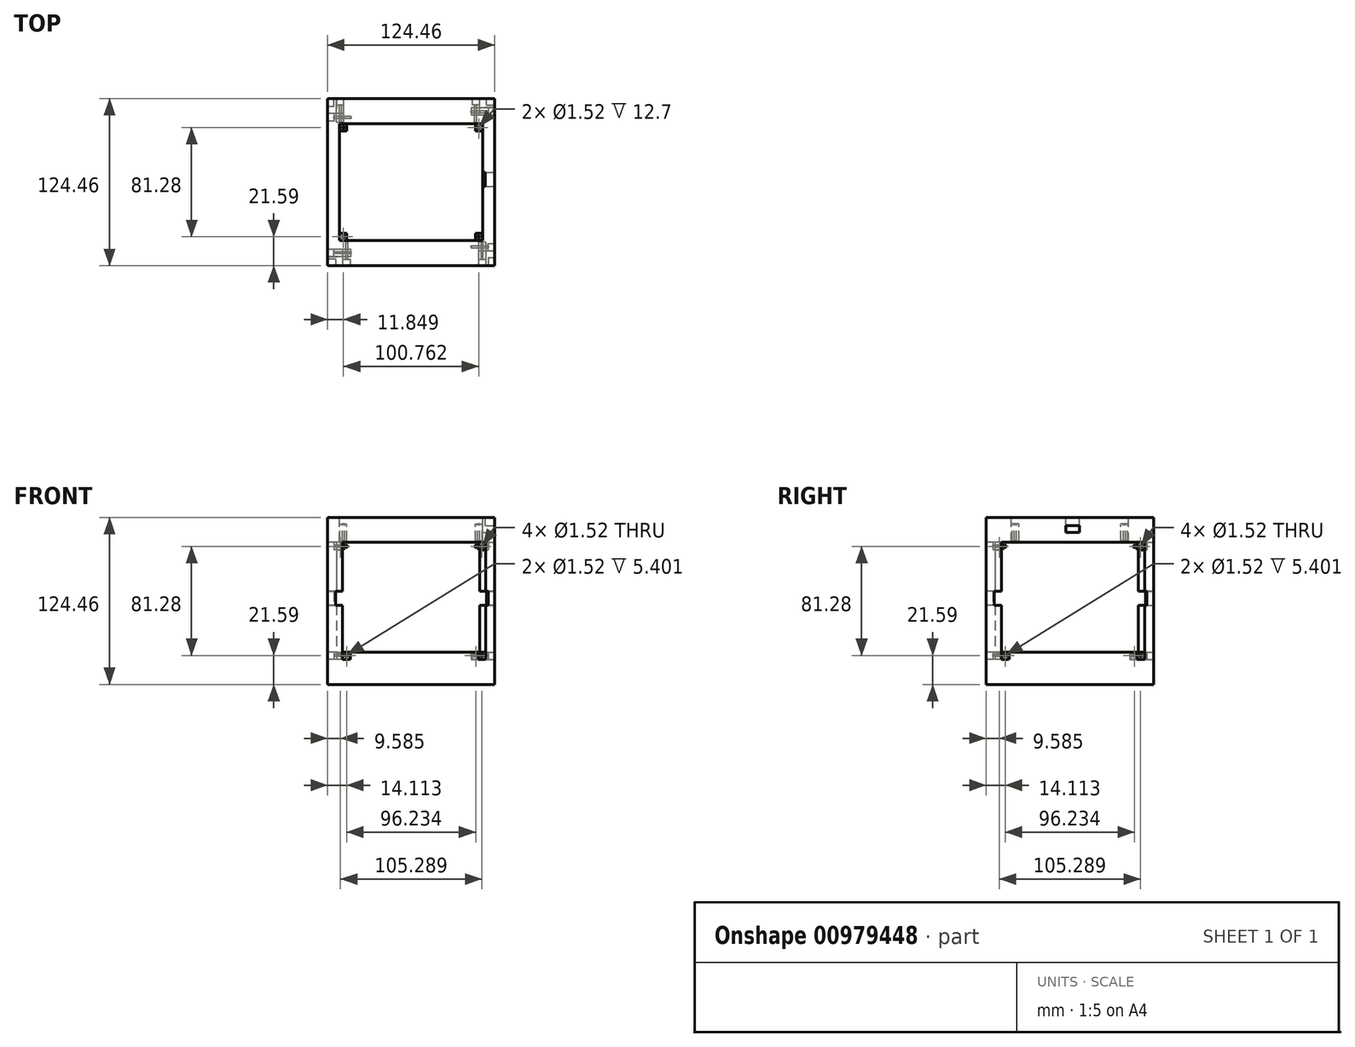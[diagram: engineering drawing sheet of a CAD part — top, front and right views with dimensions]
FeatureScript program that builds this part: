
annotation { "Feature Type Name" : "Feature", "Feature Type Description" : "" }
export const myFeature = defineFeature(function(context is Context, id is Id, definition is map)
    precondition{}
    {
        {
            var Q0;
            Q0=qCreatedBy(makeId("Top.planeOp"),FACE);
            var sketch = newSketch(context, id + "F0", { "sketchPlane" : qUnion([Q0])});
            skLineSegment(sketch, "E0.bottom", {"start": v(62.23, -62.23) * mm, "end": v(-62.23, -62.23) * mm});
            skLineSegment(sketch, "E0.top", {"start": v(62.23, 62.23) * mm, "end": v(-62.23, 62.23) * mm});
            skLineSegment(sketch, "E0.left", {"start": v(62.23, -62.23) * mm, "end": v(62.23, 62.23) * mm});
            skLineSegment(sketch, "E0.right", {"start": v(-62.23, -62.23) * mm, "end": v(-62.23, 62.23) * mm});
            skSolve(sketch);
        }
        {
            var Q0;
            Q0=makeQuery(id+"F0.imprint","IMPRINT",FACE,{"disambiguationData":[TD([[makeQuery(id+"F0.imprint","IMPRINT",EDGE,{"derivedFrom":sQuery(id+"F0.wireOp",EDGE,"E0.bottom")}),-1.0]])]});
            extrude(context, id + "F1", {"entities" : qUnion([Q0]), "depth" : 124.46 * mm, "offsetDistance" : 25.4 * mm});
        }
        {
            var Q0;
            Q0=makeQuery(id+"F1.opExtrude","CAP_FACE",FACE,{"disambiguationData":[OSD([sQuery(id+"F0.wireOp",EDGE,"E0.bottom"),sQuery(id+"F0.wireOp",EDGE,"E0.top"),sQuery(id+"F0.wireOp",EDGE,"E0.left"),sQuery(id+"F0.wireOp",EDGE,"E0.right")])],"isStart":false});
            var sketch = newSketch(context, id + "F2", { "sketchPlane" : qUnion([Q0])});
            skLineSegment(sketch, "E1.bottom", {"start": v(-52.92, 43.18) * mm, "end": v(52.92, 43.18) * mm});
            skLineSegment(sketch, "E1.top", {"start": v(-52.92, -43.18) * mm, "end": v(52.92, -43.18) * mm});
            skLineSegment(sketch, "E1.left", {"start": v(-52.92, 43.18) * mm, "end": v(-52.92, -43.18) * mm});
            skLineSegment(sketch, "E1.right", {"start": v(52.92, 43.18) * mm, "end": v(52.92, -43.18) * mm});
            skPoint(sketch, "E1.middle", {"position": v(0, 0) * mm});
            skCircle(sketch, "E2", {"center": v(-50.38, -40.64) * mm, "radius": 0.76 * mm});
            skCircle(sketch, "E3.MirrorC", {"center": v(50.38, -40.64) * mm, "radius": 0.76 * mm});
            skCircle(sketch, "E4.MirrorC", {"center": v(-50.38, 40.64) * mm, "radius": 0.76 * mm});
            skCircle(sketch, "E5.MirrorC", {"center": v(50.38, 40.64) * mm, "radius": 0.76 * mm});
            skLineSegment(sketch, "E6.0", {"start": v(-53.32, 43.58) * mm, "end": v(-53.32, -43.58) * mm});
            skLineSegment(sketch, "E6.1", {"start": v(-53.32, 43.58) * mm, "end": v(53.32, 43.58) * mm});
            skLineSegment(sketch, "E6.2", {"start": v(53.32, 43.58) * mm, "end": v(53.32, -43.58) * mm});
            skLineSegment(sketch, "E6.3", {"start": v(-53.32, -43.58) * mm, "end": v(53.32, -43.58) * mm});
            skLineSegment(sketch, "E7.top", {"start": v(53.32, -38.1) * mm, "end": v(47.84, -38.1) * mm});
            skLineSegment(sketch, "E7.right", {"start": v(47.84, -43.58) * mm, "end": v(47.84, -38.1) * mm});
            skLineSegment(sketch, "E8.MirrorCS", {"start": v(47.84, 43.58) * mm, "end": v(47.84, 38.1) * mm});
            skLineSegment(sketch, "E9.MirrorCS", {"start": v(53.32, 38.1) * mm, "end": v(47.84, 38.1) * mm});
            skLineSegment(sketch, "E10.MirrorCS", {"start": v(-53.32, -38.1) * mm, "end": v(-47.84, -38.1) * mm});
            skLineSegment(sketch, "E11.MirrorCS", {"start": v(-47.84, -43.58) * mm, "end": v(-47.84, -38.1) * mm});
            skLineSegment(sketch, "E12.MirrorCS", {"start": v(-53.32, 38.1) * mm, "end": v(-47.84, 38.1) * mm});
            skLineSegment(sketch, "E13.MirrorCS", {"start": v(-47.84, 43.58) * mm, "end": v(-47.84, 38.1) * mm});
            skLineSegment(sketch, "E14.MirrorCS", {"start": v(51.04, 6.8) * mm, "end": v(54.8, 6.8) * mm});
            skLineSegment(sketch, "E15.MirrorCS", {"start": v(51.04, -3.13) * mm, "end": v(55.2, -3.13) * mm});
            skLineSegment(sketch, "E16.MirrorCS", {"start": v(51.04, -2.73) * mm, "end": v(54.8, -2.73) * mm});
            skLineSegment(sketch, "E17.MirrorCS", {"start": v(55.2, 7.2) * mm, "end": v(55.2, -3.13) * mm});
            skLineSegment(sketch, "E18.MirrorCS", {"start": v(51.04, 7.2) * mm, "end": v(55.2, 7.2) * mm});
            skLineSegment(sketch, "E19.MirrorCS", {"start": v(54.8, 6.8) * mm, "end": v(54.8, -2.73) * mm});
            skPoint(sketch, "E20.MirrorP", {"position": v(52.92, 2.03) * mm});
            skLineSegment(sketch, "E21.bottom", {"start": v(-62.23, -62.23) * mm, "end": v(62.23, -62.23) * mm});
            skLineSegment(sketch, "E21.top", {"start": v(-62.23, 62.23) * mm, "end": v(62.23, 62.23) * mm});
            skLineSegment(sketch, "E21.left", {"start": v(-62.23, -62.23) * mm, "end": v(-62.23, 62.23) * mm});
            skLineSegment(sketch, "E21.right", {"start": v(62.23, -62.23) * mm, "end": v(62.23, 62.23) * mm});
            skSolve(sketch);
        }
        {
            var Q0;
            Q0=makeQuery(id+"F2.imprint","IMPRINT",FACE,{"disambiguationData":[TD([[makeQuery(id+"F2.imprint","IMPRINT",EDGE,{"derivedFrom":sQuery(id+"F2.wireOp",EDGE,"E2")}),-1.0]])]});
            var Q1;
            {var subQ5=sQuery(id+"F2.wireOp",EDGE,"E1.left");var subQ6=sQuery(id+"F2.wireOp",EDGE,"E1.top");var subQ7=makeQuery(id+"F2.imprint","INTERSECT",VERTEX,{"derivedFrom":[subQ6,subQ5]});Q1=makeQuery(id+"F2.imprint","IMPRINT",FACE,{"disambiguationData":[TD([[makeQuery(id+"F2.imprint","IMPRINT",EDGE,{"disambiguationData":[TD([[subQ7,-1.0]])],"derivedFrom":subQ6}),-1.0]])]});}
            var Q2;
            {var subQ7=sQuery(id+"F2.wireOp",EDGE,"E1.right");var subQ8=sQuery(id+"F2.wireOp",EDGE,"E1.top");var subQ9=makeQuery(id+"F2.imprint","INTERSECT",VERTEX,{"derivedFrom":[subQ8,subQ7]});Q2=makeQuery(id+"F2.imprint","IMPRINT",FACE,{"disambiguationData":[TD([[makeQuery(id+"F2.imprint","IMPRINT",EDGE,{"disambiguationData":[TD([[subQ9,1.0]])],"derivedFrom":subQ8}),-1.0]])]});}
            var Q3;
            Q3=makeQuery(id+"F2.imprint","IMPRINT",FACE,{"disambiguationData":[TD([[makeQuery(id+"F2.imprint","IMPRINT",EDGE,{"derivedFrom":sQuery(id+"F2.wireOp",EDGE,"E3.MirrorC")}),1.0]])]});
            var Q4;
            {var subQ7=sQuery(id+"F2.wireOp",EDGE,"E1.right");var subQ8=sQuery(id+"F2.wireOp",EDGE,"E1.bottom");var subQ9=makeQuery(id+"F2.imprint","INTERSECT",VERTEX,{"derivedFrom":[subQ8,subQ7]});Q4=makeQuery(id+"F2.imprint","IMPRINT",FACE,{"disambiguationData":[TD([[makeQuery(id+"F2.imprint","IMPRINT",EDGE,{"disambiguationData":[TD([[subQ9,1.0]])],"derivedFrom":subQ8}),1.0]])]});}
            var Q5;
            Q5=makeQuery(id+"F2.imprint","IMPRINT",FACE,{"disambiguationData":[TD([[makeQuery(id+"F2.imprint","IMPRINT",EDGE,{"derivedFrom":sQuery(id+"F2.wireOp",EDGE,"E5.MirrorC")}),-1.0]])]});
            var Q6;
            {var subQ5=sQuery(id+"F2.wireOp",EDGE,"E1.left");var subQ6=sQuery(id+"F2.wireOp",EDGE,"E1.bottom");var subQ7=makeQuery(id+"F2.imprint","INTERSECT",VERTEX,{"derivedFrom":[subQ6,subQ5]});Q6=makeQuery(id+"F2.imprint","IMPRINT",FACE,{"disambiguationData":[TD([[makeQuery(id+"F2.imprint","IMPRINT",EDGE,{"disambiguationData":[TD([[subQ7,-1.0]])],"derivedFrom":subQ6}),1.0]])]});}
            var Q7;
            Q7=makeQuery(id+"F2.imprint","IMPRINT",FACE,{"disambiguationData":[TD([[makeQuery(id+"F2.imprint","IMPRINT",EDGE,{"derivedFrom":sQuery(id+"F2.wireOp",EDGE,"E4.MirrorC")}),1.0]])]});
            extrude(context, id + "F3", {"entities" : qUnion([Q0, Q1, Q2, Q3, Q4, Q5, Q6, Q7]), "operationType" : NewBodyOperationType.REMOVE, "oppositeDirection" : true, "depth" : 4.83 * mm, "offsetDistance" : 25.4 * mm});
        }
        {
            var Q0;
            {var subQ20=sQuery(id+"F2.wireOp",EDGE,"E1.bottom");var subQ22=sQuery(id+"F2.wireOp",EDGE,"E13.MirrorCS");var subQ23=makeQuery(id+"F2.imprint","INTERSECT",VERTEX,{"derivedFrom":[subQ20,subQ22]});Q0=makeQuery(id+"F2.imprint","IMPRINT",FACE,{"disambiguationData":[TD([[makeQuery(id+"F2.imprint","IMPRINT",EDGE,{"disambiguationData":[TD([[subQ23,-1.0]])],"derivedFrom":subQ20}),-1.0]])]});}
            var Q1;
            {var subQ0=sQuery(id+"F2.wireOp",EDGE,"E13.MirrorCS");var subQ1=sQuery(id+"F2.wireOp",EDGE,"E1.bottom");var subQ2=makeQuery(id+"F2.imprint","INTERSECT",VERTEX,{"derivedFrom":[subQ1,subQ0]});Q1=makeQuery(id+"F2.imprint","IMPRINT",FACE,{"disambiguationData":[TD([[makeQuery(id+"F2.imprint","IMPRINT",EDGE,{"disambiguationData":[TD([[subQ2,-1.0]])],"derivedFrom":subQ1}),1.0]])]});}
            var Q2;
            {var subQ0=sQuery(id+"F2.wireOp",EDGE,"59694670-6818-448a-b48b-58002c6f26f5.2");var subQ1=sQuery(id+"F2.wireOp",EDGE,"E1.left");var subQ2=makeQuery(id+"F2.imprint","INTERSECT",VERTEX,{"derivedFrom":[subQ1,subQ0]});Q2=makeQuery(id+"F2.imprint","IMPRINT",FACE,{"disambiguationData":[TD([[makeQuery(id+"F2.imprint","IMPRINT",EDGE,{"disambiguationData":[TD([[subQ2,1.0]])],"derivedFrom":subQ1}),-1.0]])]});}
            var Q3;
            {var subQ0=sQuery(id+"F2.wireOp",EDGE,"E9.MirrorCS");var subQ1=sQuery(id+"F2.wireOp",EDGE,"E1.right");var subQ2=makeQuery(id+"F2.imprint","INTERSECT",VERTEX,{"derivedFrom":[subQ1,subQ0]});Q3=makeQuery(id+"F2.imprint","IMPRINT",FACE,{"disambiguationData":[TD([[makeQuery(id+"F2.imprint","IMPRINT",EDGE,{"disambiguationData":[TD([[subQ2,-1.0]])],"derivedFrom":subQ1}),1.0]])]});}
            var Q4;
            {var subQ0=sQuery(id+"F2.wireOp",EDGE,"E11.MirrorCS");var subQ1=sQuery(id+"F2.wireOp",EDGE,"E1.top");var subQ2=makeQuery(id+"F2.imprint","INTERSECT",VERTEX,{"derivedFrom":[subQ1,subQ0]});Q4=makeQuery(id+"F2.imprint","IMPRINT",FACE,{"disambiguationData":[TD([[makeQuery(id+"F2.imprint","IMPRINT",EDGE,{"disambiguationData":[TD([[subQ2,-1.0]])],"derivedFrom":subQ1}),-1.0]])]});}
            var Q5;
            {var subQ0=sQuery(id+"F2.wireOp",EDGE,"01Z94Qzt-EJPi-t4h5-vXe4-wsMJar4ZymQo.bottom");var subQ1=sQuery(id+"F2.wireOp",EDGE,"E1.left");var subQ2=makeQuery(id+"F2.imprint","INTERSECT",VERTEX,{"derivedFrom":[subQ1,subQ0]});Q5=makeQuery(id+"F2.imprint","IMPRINT",FACE,{"disambiguationData":[TD([[makeQuery(id+"F2.imprint","IMPRINT",EDGE,{"disambiguationData":[TD([[subQ2,-1.0]])],"derivedFrom":subQ1}),-1.0]])]});}
            var Q6;
            {var subQ0=sQuery(id+"F2.wireOp",EDGE,"59694670-6818-448a-b48b-58002c6f26f5.2");var subQ1=sQuery(id+"F2.wireOp",EDGE,"E1.left");var subQ2=makeQuery(id+"F2.imprint","INTERSECT",VERTEX,{"derivedFrom":[subQ1,subQ0]});Q6=makeQuery(id+"F2.imprint","IMPRINT",FACE,{"disambiguationData":[TD([[makeQuery(id+"F2.imprint","IMPRINT",EDGE,{"disambiguationData":[TD([[subQ2,-1.0]])],"derivedFrom":subQ1}),-1.0]])]});}
            var Q7;
            {var subQ0=sQuery(id+"F2.wireOp",EDGE,"01Z94Qzt-EJPi-t4h5-vXe4-wsMJar4ZymQo.top");var subQ1=sQuery(id+"F2.wireOp",EDGE,"E1.left");var subQ2=makeQuery(id+"F2.imprint","INTERSECT",VERTEX,{"derivedFrom":[subQ1,subQ0]});Q7=makeQuery(id+"F2.imprint","IMPRINT",FACE,{"disambiguationData":[TD([[makeQuery(id+"F2.imprint","IMPRINT",EDGE,{"disambiguationData":[TD([[subQ2,-1.0]])],"derivedFrom":subQ1}),-1.0]])]});}
            var Q8;
            {var subQ0=sQuery(id+"F2.wireOp",EDGE,"59694670-6818-448a-b48b-58002c6f26f5.0");var subQ1=sQuery(id+"F2.wireOp",EDGE,"E1.left");var subQ2=makeQuery(id+"F2.imprint","INTERSECT",VERTEX,{"derivedFrom":[subQ1,subQ0]});Q8=makeQuery(id+"F2.imprint","IMPRINT",FACE,{"disambiguationData":[TD([[makeQuery(id+"F2.imprint","IMPRINT",EDGE,{"disambiguationData":[TD([[subQ2,-1.0]])],"derivedFrom":subQ1}),-1.0]])]});}
            var Q9;
            {var subQ0=sQuery(id+"F2.wireOp",EDGE,"E18.MirrorCS");var subQ1=sQuery(id+"F2.wireOp",EDGE,"E1.right");var subQ2=makeQuery(id+"F2.imprint","INTERSECT",VERTEX,{"derivedFrom":[subQ1,subQ0]});Q9=makeQuery(id+"F2.imprint","IMPRINT",FACE,{"disambiguationData":[TD([[makeQuery(id+"F2.imprint","IMPRINT",EDGE,{"disambiguationData":[TD([[subQ2,-1.0]])],"derivedFrom":subQ1}),1.0]])]});}
            var Q10;
            {var subQ0=sQuery(id+"F2.wireOp",EDGE,"E14.MirrorCS");var subQ1=sQuery(id+"F2.wireOp",EDGE,"E1.right");var subQ2=makeQuery(id+"F2.imprint","INTERSECT",VERTEX,{"derivedFrom":[subQ1,subQ0]});Q10=makeQuery(id+"F2.imprint","IMPRINT",FACE,{"disambiguationData":[TD([[makeQuery(id+"F2.imprint","IMPRINT",EDGE,{"disambiguationData":[TD([[subQ2,-1.0]])],"derivedFrom":subQ1}),1.0]])]});}
            var Q11;
            {var subQ0=sQuery(id+"F2.wireOp",EDGE,"E16.MirrorCS");var subQ1=sQuery(id+"F2.wireOp",EDGE,"E1.right");var subQ2=makeQuery(id+"F2.imprint","INTERSECT",VERTEX,{"derivedFrom":[subQ1,subQ0]});Q11=makeQuery(id+"F2.imprint","IMPRINT",FACE,{"disambiguationData":[TD([[makeQuery(id+"F2.imprint","IMPRINT",EDGE,{"disambiguationData":[TD([[subQ2,-1.0]])],"derivedFrom":subQ1}),1.0]])]});}
            var Q12;
            {var subQ0=sQuery(id+"F2.wireOp",EDGE,"E15.MirrorCS");var subQ1=sQuery(id+"F2.wireOp",EDGE,"E1.right");var subQ2=makeQuery(id+"F2.imprint","INTERSECT",VERTEX,{"derivedFrom":[subQ1,subQ0]});Q12=makeQuery(id+"F2.imprint","IMPRINT",FACE,{"disambiguationData":[TD([[makeQuery(id+"F2.imprint","IMPRINT",EDGE,{"disambiguationData":[TD([[subQ2,-1.0]])],"derivedFrom":subQ1}),1.0]])]});}
            extrude(context, id + "F4", {"entities" : qUnion([Q0, Q1, Q2, Q3, Q4, Q5, Q6, Q7, Q8, Q9, Q10, Q11, Q12]), "operationType" : NewBodyOperationType.REMOVE, "oppositeDirection" : true, "depth" : 25.4 * mm, "offsetDistance" : 25.4 * mm});
        }
        {
            var Q0;
            Q0=makeQuery(id+"F1.opExtrude","SWEPT_FACE",FACE,{"disambiguationData":[OSD([sQuery(id+"F0.wireOp",EDGE,"E0.bottom")])]});
            var sketch = newSketch(context, id + "F5", { "sketchPlane" : qUnion([Q0])});
            skPoint(sketch, "E22.middle", {"position": v(2.26, 62.23) * mm});
            skCircle(sketch, "E23", {"center": v(-48.12, 21.6) * mm, "radius": 0.76 * mm});
            skCircle(sketch, "E24.MirrorC", {"center": v(52.64, 21.6) * mm, "radius": 0.76 * mm});
            skCircle(sketch, "E25.MirrorC", {"center": v(-48.12, 102.87) * mm, "radius": 0.76 * mm});
            skCircle(sketch, "E26.MirrorC", {"center": v(52.64, 102.87) * mm, "radius": 0.76 * mm});
            skLineSegment(sketch, "E27.0", {"start": v(-51.05, 105.8) * mm, "end": v(-51.05, 18.65) * mm});
            skLineSegment(sketch, "E27.1", {"start": v(-51.05, 105.8) * mm, "end": v(55.58, 105.8) * mm});
            skLineSegment(sketch, "E27.2", {"start": v(55.58, 105.8) * mm, "end": v(55.58, 18.65) * mm});
            skLineSegment(sketch, "E27.3", {"start": v(-51.05, 18.65) * mm, "end": v(55.58, 18.65) * mm});
            skLineSegment(sketch, "E28.top", {"start": v(55.58, 24.13) * mm, "end": v(50.1, 24.13) * mm});
            skLineSegment(sketch, "E28.right", {"start": v(50.1, 18.65) * mm, "end": v(50.1, 24.13) * mm});
            skLineSegment(sketch, "E29.MirrorCS", {"start": v(50.1, 105.8) * mm, "end": v(50.1, 100.33) * mm});
            skLineSegment(sketch, "E30.MirrorCS", {"start": v(55.58, 100.33) * mm, "end": v(50.1, 100.33) * mm});
            skLineSegment(sketch, "E31.MirrorCS", {"start": v(-51.05, 24.13) * mm, "end": v(-45.58, 24.13) * mm});
            skLineSegment(sketch, "E32.MirrorCS", {"start": v(-45.58, 18.65) * mm, "end": v(-45.58, 24.13) * mm});
            skLineSegment(sketch, "E33.MirrorCS", {"start": v(-51.05, 100.33) * mm, "end": v(-45.58, 100.33) * mm});
            skLineSegment(sketch, "E34.MirrorCS", {"start": v(-45.58, 105.8) * mm, "end": v(-45.58, 100.33) * mm});
            skLineSegment(sketch, "E35.MirrorCS", {"start": v(53.3, 59.1) * mm, "end": v(57.46, 59.1) * mm});
            skLineSegment(sketch, "E36.MirrorCS", {"start": v(57.46, 69.42) * mm, "end": v(57.46, 59.1) * mm});
            skLineSegment(sketch, "E37.MirrorCS", {"start": v(53.3, 69.42) * mm, "end": v(57.46, 69.42) * mm});
            skPoint(sketch, "E38.MirrorP", {"position": v(55.18, 64.26) * mm});
            skPoint(sketch, "E39", {"position": v(-62.23, 62.23) * mm});
            skLineSegment(sketch, "E40.bottom", {"start": v(-62.23, 0) * mm, "end": v(62.23, 0) * mm});
            skLineSegment(sketch, "E40.top", {"start": v(-62.23, 124.46) * mm, "end": v(62.23, 124.46) * mm});
            skLineSegment(sketch, "E40.left", {"start": v(-62.23, 0) * mm, "end": v(-62.23, 124.46) * mm});
            skLineSegment(sketch, "E40.right", {"start": v(59.41, 0) * mm, "end": v(59.41, 124.46) * mm});
            skLineSegment(sketch, "E41.bottom", {"start": v(-62.23, 59.1) * mm, "end": v(-51.05, 59.1) * mm});
            skLineSegment(sketch, "E41.top", {"start": v(-62.23, 69.42) * mm, "end": v(-51.05, 69.42) * mm});
            skLineSegment(sketch, "E41.left", {"start": v(-62.23, 59.1) * mm, "end": v(-62.23, 69.42) * mm});
            skLineSegment(sketch, "E41.right", {"start": v(-51.05, 59.1) * mm, "end": v(-51.05, 69.42) * mm});
            skLineSegment(sketch, "E42", {"start": v(-56.25, 69.42) * mm, "end": v(-56.25, 59.1) * mm});
            skLineSegment(sketch, "E43", {"start": v(-45.58, 24.13) * mm, "end": v(50.1, 24.13) * mm});
            skSolve(sketch);
        }
        {
            var Q0;
            Q0=makeQuery(id+"F1.opExtrude","SWEPT_FACE",FACE,{"disambiguationData":[OSD([sQuery(id+"F0.wireOp",EDGE,"E0.left")])]});
            var sketch = newSketch(context, id + "F6", { "sketchPlane" : qUnion([Q0])});
            skPoint(sketch, "E44.middle", {"position": v(2.26, 62.23) * mm});
            skCircle(sketch, "E45", {"center": v(-48.12, 21.59) * mm, "radius": 0.76 * mm});
            skCircle(sketch, "E46.MirrorC", {"center": v(52.64, 21.59) * mm, "radius": 0.76 * mm});
            skCircle(sketch, "E47.MirrorC", {"center": v(-48.12, 102.87) * mm, "radius": 0.76 * mm});
            skCircle(sketch, "E48.MirrorC", {"center": v(52.64, 102.87) * mm, "radius": 0.76 * mm});
            skLineSegment(sketch, "E49.0", {"start": v(-51.05, 105.8) * mm, "end": v(-51.05, 18.65) * mm});
            skLineSegment(sketch, "E49.1", {"start": v(-51.05, 105.8) * mm, "end": v(55.58, 105.8) * mm});
            skLineSegment(sketch, "E49.2", {"start": v(55.58, 105.8) * mm, "end": v(55.58, 18.65) * mm});
            skLineSegment(sketch, "E49.3", {"start": v(-51.05, 18.65) * mm, "end": v(55.58, 18.65) * mm});
            skLineSegment(sketch, "E50.top", {"start": v(55.58, 24.13) * mm, "end": v(50.1, 24.13) * mm});
            skLineSegment(sketch, "E50.right", {"start": v(50.1, 18.65) * mm, "end": v(50.1, 24.13) * mm});
            skLineSegment(sketch, "E51.MirrorCS", {"start": v(50.1, 105.8) * mm, "end": v(50.1, 100.33) * mm});
            skLineSegment(sketch, "E52.MirrorCS", {"start": v(55.58, 100.33) * mm, "end": v(50.1, 100.33) * mm});
            skLineSegment(sketch, "E53.MirrorCS", {"start": v(-51.05, 24.13) * mm, "end": v(-45.58, 24.13) * mm});
            skLineSegment(sketch, "E54.MirrorCS", {"start": v(-45.58, 18.65) * mm, "end": v(-45.58, 24.13) * mm});
            skLineSegment(sketch, "E55.MirrorCS", {"start": v(-51.05, 100.33) * mm, "end": v(-45.58, 100.33) * mm});
            skLineSegment(sketch, "E56.MirrorCS", {"start": v(-45.58, 105.8) * mm, "end": v(-45.58, 100.33) * mm});
            skLineSegment(sketch, "E57.MirrorCS", {"start": v(53.3, 59.1) * mm, "end": v(57.46, 59.1) * mm});
            skLineSegment(sketch, "E58.MirrorCS", {"start": v(57.46, 69.42) * mm, "end": v(57.46, 59.1) * mm});
            skLineSegment(sketch, "E59.MirrorCS", {"start": v(53.3, 69.42) * mm, "end": v(57.46, 69.42) * mm});
            skPoint(sketch, "E60.MirrorP", {"position": v(55.18, 64.26) * mm});
            skPoint(sketch, "E61", {"position": v(-62.23, 62.23) * mm});
            skLineSegment(sketch, "E62.bottom", {"start": v(-62.23, 0) * mm, "end": v(62.23, 0) * mm});
            skLineSegment(sketch, "E62.top", {"start": v(-62.23, 124.46) * mm, "end": v(62.23, 124.46) * mm});
            skLineSegment(sketch, "E62.left", {"start": v(-62.23, 0) * mm, "end": v(-62.23, 124.46) * mm});
            skLineSegment(sketch, "E62.right", {"start": v(62.23, 0) * mm, "end": v(62.23, 124.46) * mm});
            skLineSegment(sketch, "E63.bottom", {"start": v(-62.23, 59.1) * mm, "end": v(-51.05, 59.1) * mm});
            skLineSegment(sketch, "E63.top", {"start": v(-62.23, 69.42) * mm, "end": v(-51.05, 69.42) * mm});
            skLineSegment(sketch, "E63.left", {"start": v(-62.23, 59.1) * mm, "end": v(-62.23, 69.42) * mm});
            skLineSegment(sketch, "E63.right", {"start": v(-51.05, 59.1) * mm, "end": v(-51.05, 69.42) * mm});
            skLineSegment(sketch, "E64", {"start": v(-56.25, 69.42) * mm, "end": v(-56.25, 59.1) * mm});
            skPoint(sketch, "E65", {"position": v(-0.1, 124.46) * mm});
            skLineSegment(sketch, "E66.bottom", {"start": v(-3.13, 124.46) * mm, "end": v(-3.13, 113.28) * mm});
            skLineSegment(sketch, "E66.top", {"start": v(7.2, 124.46) * mm, "end": v(7.2, 113.28) * mm});
            skLineSegment(sketch, "E66.left", {"start": v(-3.13, 124.46) * mm, "end": v(7.2, 124.46) * mm});
            skLineSegment(sketch, "E66.right", {"start": v(-3.13, 113.28) * mm, "end": v(7.2, 113.28) * mm});
            skLineSegment(sketch, "E67", {"start": v(7.2, 118.48) * mm, "end": v(-3.13, 118.48) * mm});
            skLineSegment(sketch, "E68", {"start": v(-45.58, 24.13) * mm, "end": v(50.1, 24.13) * mm});
            skSolve(sketch);
        }
        {
            var Q0;
            Q0=makeQuery(id+"F1.opExtrude","SWEPT_FACE",FACE,{"disambiguationData":[OSD([sQuery(id+"F0.wireOp",EDGE,"E0.top")])]});
            var sketch = newSketch(context, id + "F7", { "sketchPlane" : qUnion([Q0])});
            skPoint(sketch, "E69.middle", {"position": v(2.26, 62.23) * mm});
            skCircle(sketch, "E70", {"center": v(-48.12, 21.59) * mm, "radius": 0.76 * mm});
            skCircle(sketch, "E71.MirrorC", {"center": v(52.64, 21.59) * mm, "radius": 0.76 * mm});
            skCircle(sketch, "E72.MirrorC", {"center": v(-48.12, 102.87) * mm, "radius": 0.76 * mm});
            skCircle(sketch, "E73.MirrorC", {"center": v(52.64, 102.87) * mm, "radius": 0.76 * mm});
            skLineSegment(sketch, "E74.0", {"start": v(-51.05, 105.8) * mm, "end": v(-51.05, 18.65) * mm});
            skLineSegment(sketch, "E74.1", {"start": v(-51.05, 105.8) * mm, "end": v(55.58, 105.8) * mm});
            skLineSegment(sketch, "E74.2", {"start": v(55.58, 105.8) * mm, "end": v(55.58, 18.65) * mm});
            skLineSegment(sketch, "E74.3", {"start": v(-51.05, 18.65) * mm, "end": v(55.58, 18.65) * mm});
            skLineSegment(sketch, "E75.top", {"start": v(55.58, 24.13) * mm, "end": v(50.1, 24.13) * mm});
            skLineSegment(sketch, "E75.right", {"start": v(50.1, 18.65) * mm, "end": v(50.1, 24.13) * mm});
            skLineSegment(sketch, "E76.MirrorCS", {"start": v(50.1, 105.8) * mm, "end": v(50.1, 100.33) * mm});
            skLineSegment(sketch, "E77.MirrorCS", {"start": v(55.58, 100.33) * mm, "end": v(50.1, 100.33) * mm});
            skLineSegment(sketch, "E78.MirrorCS", {"start": v(-51.05, 24.13) * mm, "end": v(-45.58, 24.13) * mm});
            skLineSegment(sketch, "E79.MirrorCS", {"start": v(-45.58, 18.65) * mm, "end": v(-45.58, 24.13) * mm});
            skLineSegment(sketch, "E80.MirrorCS", {"start": v(-51.05, 100.33) * mm, "end": v(-45.58, 100.33) * mm});
            skLineSegment(sketch, "E81.MirrorCS", {"start": v(-45.58, 105.8) * mm, "end": v(-45.58, 100.33) * mm});
            skLineSegment(sketch, "E82.MirrorCS", {"start": v(53.3, 59.1) * mm, "end": v(57.46, 59.1) * mm});
            skLineSegment(sketch, "E83.MirrorCS", {"start": v(57.46, 69.42) * mm, "end": v(57.46, 59.1) * mm});
            skLineSegment(sketch, "E84.MirrorCS", {"start": v(53.3, 69.42) * mm, "end": v(57.46, 69.42) * mm});
            skPoint(sketch, "E85.MirrorP", {"position": v(55.18, 64.26) * mm});
            skPoint(sketch, "E86", {"position": v(-62.23, 62.23) * mm});
            skLineSegment(sketch, "E87.bottom", {"start": v(-62.23, 0) * mm, "end": v(62.23, 0) * mm});
            skLineSegment(sketch, "E87.top", {"start": v(-62.23, 124.46) * mm, "end": v(62.23, 124.46) * mm});
            skLineSegment(sketch, "E87.left", {"start": v(-62.23, 0) * mm, "end": v(-62.23, 124.46) * mm});
            skLineSegment(sketch, "E87.right", {"start": v(62.23, 0) * mm, "end": v(62.23, 124.46) * mm});
            skLineSegment(sketch, "E88.bottom", {"start": v(-62.23, 59.1) * mm, "end": v(-51.05, 59.1) * mm});
            skLineSegment(sketch, "E88.top", {"start": v(-62.23, 69.42) * mm, "end": v(-51.05, 69.42) * mm});
            skLineSegment(sketch, "E88.left", {"start": v(-62.23, 59.1) * mm, "end": v(-62.23, 69.42) * mm});
            skLineSegment(sketch, "E88.right", {"start": v(-51.05, 59.1) * mm, "end": v(-51.05, 69.42) * mm});
            skLineSegment(sketch, "E89", {"start": v(-56.25, 69.42) * mm, "end": v(-56.25, 59.1) * mm});
            skLineSegment(sketch, "E90", {"start": v(-45.58, 24.13) * mm, "end": v(50.1, 24.13) * mm});
            skSolve(sketch);
        }
        {
            var Q0;
            Q0=makeQuery(id+"F1.opExtrude","SWEPT_FACE",FACE,{"disambiguationData":[OSD([sQuery(id+"F0.wireOp",EDGE,"E0.right")])]});
            var sketch = newSketch(context, id + "F8", { "sketchPlane" : qUnion([Q0])});
            skPoint(sketch, "E91.middle", {"position": v(2.26, 62.23) * mm});
            skCircle(sketch, "E92", {"center": v(-48.12, 21.59) * mm, "radius": 0.76 * mm});
            skCircle(sketch, "E93.MirrorC", {"center": v(52.64, 21.59) * mm, "radius": 0.76 * mm});
            skCircle(sketch, "E94.MirrorC", {"center": v(-48.12, 102.87) * mm, "radius": 0.76 * mm});
            skCircle(sketch, "E95.MirrorC", {"center": v(52.64, 102.87) * mm, "radius": 0.76 * mm});
            skLineSegment(sketch, "E96.0", {"start": v(-51.05, 105.8) * mm, "end": v(-51.05, 18.65) * mm});
            skLineSegment(sketch, "E96.1", {"start": v(-51.05, 105.8) * mm, "end": v(55.58, 105.8) * mm});
            skLineSegment(sketch, "E96.2", {"start": v(55.58, 105.8) * mm, "end": v(55.58, 18.65) * mm});
            skLineSegment(sketch, "E96.3", {"start": v(-51.05, 18.65) * mm, "end": v(55.58, 18.65) * mm});
            skLineSegment(sketch, "E97.top", {"start": v(55.58, 24.13) * mm, "end": v(50.1, 24.13) * mm});
            skLineSegment(sketch, "E97.right", {"start": v(50.1, 18.65) * mm, "end": v(50.1, 24.13) * mm});
            skLineSegment(sketch, "E98.MirrorCS", {"start": v(50.1, 105.8) * mm, "end": v(50.1, 100.33) * mm});
            skLineSegment(sketch, "E99.MirrorCS", {"start": v(55.58, 100.33) * mm, "end": v(50.1, 100.33) * mm});
            skLineSegment(sketch, "E100.MirrorCS", {"start": v(-51.05, 24.13) * mm, "end": v(-45.58, 24.13) * mm});
            skLineSegment(sketch, "E101.MirrorCS", {"start": v(-45.58, 18.65) * mm, "end": v(-45.58, 24.13) * mm});
            skLineSegment(sketch, "E102.MirrorCS", {"start": v(-51.05, 100.33) * mm, "end": v(-45.58, 100.33) * mm});
            skLineSegment(sketch, "E103.MirrorCS", {"start": v(-45.58, 105.8) * mm, "end": v(-45.58, 100.33) * mm});
            skLineSegment(sketch, "E104.MirrorCS", {"start": v(53.3, 59.1) * mm, "end": v(57.46, 59.1) * mm});
            skLineSegment(sketch, "E105.MirrorCS", {"start": v(57.46, 69.42) * mm, "end": v(57.46, 59.1) * mm});
            skLineSegment(sketch, "E106.MirrorCS", {"start": v(53.3, 69.42) * mm, "end": v(57.46, 69.42) * mm});
            skPoint(sketch, "E107.MirrorP", {"position": v(55.18, 64.26) * mm});
            skPoint(sketch, "E108", {"position": v(-62.23, 62.23) * mm});
            skLineSegment(sketch, "E109.bottom", {"start": v(-62.23, 0) * mm, "end": v(62.23, 0) * mm});
            skLineSegment(sketch, "E109.top", {"start": v(-62.23, 124.46) * mm, "end": v(62.23, 124.46) * mm});
            skLineSegment(sketch, "E109.left", {"start": v(-62.23, 0) * mm, "end": v(-62.23, 124.46) * mm});
            skLineSegment(sketch, "E109.right", {"start": v(62.23, 0) * mm, "end": v(62.23, 124.46) * mm});
            skLineSegment(sketch, "E110.bottom", {"start": v(-62.23, 59.1) * mm, "end": v(-51.05, 59.1) * mm});
            skLineSegment(sketch, "E110.top", {"start": v(-62.23, 69.42) * mm, "end": v(-51.05, 69.42) * mm});
            skLineSegment(sketch, "E110.left", {"start": v(-62.23, 59.1) * mm, "end": v(-62.23, 69.42) * mm});
            skLineSegment(sketch, "E110.right", {"start": v(-51.05, 59.1) * mm, "end": v(-51.05, 69.42) * mm});
            skLineSegment(sketch, "E111", {"start": v(-56.25, 69.42) * mm, "end": v(-56.25, 59.1) * mm});
            skLineSegment(sketch, "E112", {"start": v(-45.58, 24.13) * mm, "end": v(50.1, 24.13) * mm});
            skSolve(sketch);
        }
        {
            var Q0;
            {var subQ5=sQuery(id+"F5.wireOp",EDGE,"E28.top");Q0=makeQuery(id+"F5.imprint","IMPRINT",FACE,{"disambiguationData":[TD([[makeQuery(id+"F5.imprint","IMPRINT",EDGE,{"derivedFrom":subQ5}),-1.0]])]});}
            var Q1;
            {var subQ5=sQuery(id+"F5.wireOp",EDGE,"E42");Q1=makeQuery(id+"F5.imprint","IMPRINT",FACE,{"disambiguationData":[TD([[makeQuery(id+"F5.imprint","IMPRINT",EDGE,{"derivedFrom":subQ5}),1.0]])]});}
            extrude(context, id + "F9", {"entities" : qUnion([Q0, Q1]), "operationType" : NewBodyOperationType.REMOVE, "oppositeDirection" : true, "depth" : 76.2 * mm, "offsetDistance" : 25.4 * mm});
        }
        {
            var Q0;
            {var subQ5=sQuery(id+"F8.wireOp",EDGE,"E97.top");Q0=makeQuery(id+"F8.imprint","IMPRINT",FACE,{"disambiguationData":[TD([[makeQuery(id+"F8.imprint","IMPRINT",EDGE,{"derivedFrom":subQ5}),-1.0]])]});}
            var Q1;
            {var subQ5=sQuery(id+"F8.wireOp",EDGE,"E111");Q1=makeQuery(id+"F8.imprint","IMPRINT",FACE,{"disambiguationData":[TD([[makeQuery(id+"F8.imprint","IMPRINT",EDGE,{"derivedFrom":subQ5}),1.0]])]});}
            extrude(context, id + "F10", {"entities" : qUnion([Q0, Q1]), "operationType" : NewBodyOperationType.REMOVE, "oppositeDirection" : true, "depth" : 76.2 * mm, "offsetDistance" : 25.4 * mm});
        }
        {
            var Q0;
            {var subQ5=sQuery(id+"F7.wireOp",EDGE,"E75.top");Q0=makeQuery(id+"F7.imprint","IMPRINT",FACE,{"disambiguationData":[TD([[makeQuery(id+"F7.imprint","IMPRINT",EDGE,{"derivedFrom":subQ5}),-1.0]])]});}
            var Q1;
            {var subQ5=sQuery(id+"F7.wireOp",EDGE,"E89");Q1=makeQuery(id+"F7.imprint","IMPRINT",FACE,{"disambiguationData":[TD([[makeQuery(id+"F7.imprint","IMPRINT",EDGE,{"derivedFrom":subQ5}),1.0]])]});}
            extrude(context, id + "F11", {"entities" : qUnion([Q0, Q1]), "operationType" : NewBodyOperationType.REMOVE, "oppositeDirection" : true, "depth" : 76.2 * mm, "offsetDistance" : 25.4 * mm});
        }
        {
            var Q0;
            {var subQ5=sQuery(id+"F6.wireOp",EDGE,"E50.top");Q0=makeQuery(id+"F6.imprint","IMPRINT",FACE,{"disambiguationData":[TD([[makeQuery(id+"F6.imprint","IMPRINT",EDGE,{"derivedFrom":subQ5}),-1.0]])]});}
            var Q1;
            {var subQ5=sQuery(id+"F6.wireOp",EDGE,"E64");Q1=makeQuery(id+"F6.imprint","IMPRINT",FACE,{"disambiguationData":[TD([[makeQuery(id+"F6.imprint","IMPRINT",EDGE,{"derivedFrom":subQ5}),1.0]])]});}
            var Q2;
            {var subQ0=sQuery(id+"F6.wireOp",EDGE,"E66.right");Q2=makeQuery(id+"F6.imprint","IMPRINT",FACE,{"disambiguationData":[TD([[makeQuery(id+"F6.imprint","IMPRINT",EDGE,{"derivedFrom":subQ0}),1.0]])]});}
            extrude(context, id + "F12", {"entities" : qUnion([Q0, Q1, Q2]), "operationType" : NewBodyOperationType.REMOVE, "oppositeDirection" : true, "depth" : 76.2 * mm, "offsetDistance" : 25.4 * mm});
        }
        {
            var Q0;
            Q0=makeQuery(id+"F5.imprint","IMPRINT",FACE,{"disambiguationData":[TD([[makeQuery(id+"F5.imprint","IMPRINT",EDGE,{"derivedFrom":sQuery(id+"F5.wireOp",EDGE,"E23")}),1.0]])]});
            var Q1;
            Q1=makeQuery(id+"F5.imprint","IMPRINT",FACE,{"disambiguationData":[TD([[makeQuery(id+"F5.imprint","IMPRINT",EDGE,{"derivedFrom":sQuery(id+"F5.wireOp",EDGE,"E24.MirrorC")}),-1.0]])]});
            var Q2;
            Q2=makeQuery(id+"F5.imprint","IMPRINT",FACE,{"disambiguationData":[TD([[makeQuery(id+"F5.imprint","IMPRINT",EDGE,{"derivedFrom":sQuery(id+"F5.wireOp",EDGE,"E26.MirrorC")}),1.0]])]});
            var Q3;
            Q3=makeQuery(id+"F5.imprint","IMPRINT",FACE,{"disambiguationData":[TD([[makeQuery(id+"F5.imprint","IMPRINT",EDGE,{"derivedFrom":sQuery(id+"F5.wireOp",EDGE,"E25.MirrorC")}),-1.0]])]});
            extrude(context, id + "F13", {"entities" : qUnion([Q0, Q1, Q2, Q3]), "operationType" : NewBodyOperationType.REMOVE, "oppositeDirection" : true, "depth" : 17.53 * mm, "offsetDistance" : 25.4 * mm});
        }
        {
            var Q0;
            Q0=makeQuery(id+"F6.imprint","IMPRINT",FACE,{"disambiguationData":[TD([[makeQuery(id+"F6.imprint","IMPRINT",EDGE,{"derivedFrom":sQuery(id+"F6.wireOp",EDGE,"E47.MirrorC")}),-1.0]])]});
            var Q1;
            Q1=makeQuery(id+"F6.imprint","IMPRINT",FACE,{"disambiguationData":[TD([[makeQuery(id+"F6.imprint","IMPRINT",EDGE,{"derivedFrom":sQuery(id+"F6.wireOp",EDGE,"E48.MirrorC")}),1.0]])]});
            var Q2;
            Q2=makeQuery(id+"F6.imprint","IMPRINT",FACE,{"disambiguationData":[TD([[makeQuery(id+"F6.imprint","IMPRINT",EDGE,{"derivedFrom":sQuery(id+"F6.wireOp",EDGE,"E46.MirrorC")}),-1.0]])]});
            var Q3;
            Q3=makeQuery(id+"F6.imprint","IMPRINT",FACE,{"disambiguationData":[TD([[makeQuery(id+"F6.imprint","IMPRINT",EDGE,{"derivedFrom":sQuery(id+"F6.wireOp",EDGE,"E45")}),1.0]])]});
            extrude(context, id + "F14", {"entities" : qUnion([Q0, Q1, Q2, Q3]), "operationType" : NewBodyOperationType.REMOVE, "oppositeDirection" : true, "depth" : 17.53 * mm, "offsetDistance" : 25.4 * mm});
        }
        {
            var Q0;
            Q0=makeQuery(id+"F7.imprint","IMPRINT",FACE,{"disambiguationData":[TD([[makeQuery(id+"F7.imprint","IMPRINT",EDGE,{"derivedFrom":sQuery(id+"F7.wireOp",EDGE,"E72.MirrorC")}),-1.0]])]});
            var Q1;
            Q1=makeQuery(id+"F7.imprint","IMPRINT",FACE,{"disambiguationData":[TD([[makeQuery(id+"F7.imprint","IMPRINT",EDGE,{"derivedFrom":sQuery(id+"F7.wireOp",EDGE,"E70")}),1.0]])]});
            var Q2;
            Q2=makeQuery(id+"F7.imprint","IMPRINT",FACE,{"disambiguationData":[TD([[makeQuery(id+"F7.imprint","IMPRINT",EDGE,{"derivedFrom":sQuery(id+"F7.wireOp",EDGE,"E71.MirrorC")}),-1.0]])]});
            var Q3;
            Q3=makeQuery(id+"F7.imprint","IMPRINT",FACE,{"disambiguationData":[TD([[makeQuery(id+"F7.imprint","IMPRINT",EDGE,{"derivedFrom":sQuery(id+"F7.wireOp",EDGE,"E73.MirrorC")}),1.0]])]});
            extrude(context, id + "F15", {"entities" : qUnion([Q0, Q1, Q2, Q3]), "operationType" : NewBodyOperationType.REMOVE, "oppositeDirection" : true, "depth" : 17.53 * mm, "offsetDistance" : 25.4 * mm});
        }
        {
            var Q0;
            Q0=makeQuery(id+"F8.imprint","IMPRINT",FACE,{"disambiguationData":[TD([[makeQuery(id+"F8.imprint","IMPRINT",EDGE,{"derivedFrom":sQuery(id+"F8.wireOp",EDGE,"E94.MirrorC")}),-1.0]])]});
            var Q1;
            Q1=makeQuery(id+"F8.imprint","IMPRINT",FACE,{"disambiguationData":[TD([[makeQuery(id+"F8.imprint","IMPRINT",EDGE,{"derivedFrom":sQuery(id+"F8.wireOp",EDGE,"E92")}),1.0]])]});
            var Q2;
            Q2=makeQuery(id+"F8.imprint","IMPRINT",FACE,{"disambiguationData":[TD([[makeQuery(id+"F8.imprint","IMPRINT",EDGE,{"derivedFrom":sQuery(id+"F8.wireOp",EDGE,"E93.MirrorC")}),-1.0]])]});
            var Q3;
            Q3=makeQuery(id+"F8.imprint","IMPRINT",FACE,{"disambiguationData":[TD([[makeQuery(id+"F8.imprint","IMPRINT",EDGE,{"derivedFrom":sQuery(id+"F8.wireOp",EDGE,"E95.MirrorC")}),1.0]])]});
            extrude(context, id + "F16", {"entities" : qUnion([Q0, Q1, Q2, Q3]), "operationType" : NewBodyOperationType.REMOVE, "oppositeDirection" : true, "depth" : 17.53 * mm, "offsetDistance" : 25.4 * mm});
        }
        {
            var Q0;
            Q0=makeQuery(id+"F2.imprint","IMPRINT",FACE,{"disambiguationData":[TD([[makeQuery(id+"F2.imprint","IMPRINT",EDGE,{"derivedFrom":sQuery(id+"F2.wireOp",EDGE,"E4.MirrorC")}),-1.0]])]});
            var Q1;
            Q1=makeQuery(id+"F2.imprint","IMPRINT",FACE,{"disambiguationData":[TD([[makeQuery(id+"F2.imprint","IMPRINT",EDGE,{"derivedFrom":sQuery(id+"F2.wireOp",EDGE,"E5.MirrorC")}),1.0]])]});
            var Q2;
            Q2=makeQuery(id+"F2.imprint","IMPRINT",FACE,{"disambiguationData":[TD([[makeQuery(id+"F2.imprint","IMPRINT",EDGE,{"derivedFrom":sQuery(id+"F2.wireOp",EDGE,"E3.MirrorC")}),-1.0]])]});
            var Q3;
            Q3=makeQuery(id+"F2.imprint","IMPRINT",FACE,{"disambiguationData":[TD([[makeQuery(id+"F2.imprint","IMPRINT",EDGE,{"derivedFrom":sQuery(id+"F2.wireOp",EDGE,"E2")}),1.0]])]});
            var Q4;
            Q4=sQuery(id+"F2.wireOp",EDGE,"E2");
            var Q5;
            Q5=sQuery(id+"F2.wireOp",EDGE,"E4.MirrorC");
            var Q6;
            Q6=sQuery(id+"F2.wireOp",EDGE,"E3.MirrorC");
            var Q7;
            Q7=sQuery(id+"F2.wireOp",EDGE,"E5.MirrorC");
            extrude(context, id + "F17", {"entities" : qUnion([Q0, Q1, Q2, Q3]), "operationType" : NewBodyOperationType.REMOVE, "surfaceEntities" : qUnion([Q4, Q5, Q6, Q7]), "oppositeDirection" : true, "depth" : 17.53 * mm, "offsetDistance" : 25.4 * mm});
        }
        {
            var Q0;
            Q0=makeQuery(id+"F7.imprint","IMPRINT",FACE,{"disambiguationData":[TD([[makeQuery(id+"F7.imprint","IMPRINT",EDGE,{"derivedFrom":sQuery(id+"F7.wireOp",EDGE,"E71.MirrorC")}),1.0]])]});
            var Q1;
            Q1=makeQuery(id+"F7.imprint","IMPRINT",FACE,{"disambiguationData":[TD([[makeQuery(id+"F7.imprint","IMPRINT",EDGE,{"derivedFrom":sQuery(id+"F7.wireOp",EDGE,"E73.MirrorC")}),-1.0]])]});
            var Q2;
            Q2=makeQuery(id+"F7.imprint","IMPRINT",FACE,{"disambiguationData":[TD([[makeQuery(id+"F7.imprint","IMPRINT",EDGE,{"derivedFrom":sQuery(id+"F7.wireOp",EDGE,"E72.MirrorC")}),1.0]])]});
            var Q3;
            Q3=makeQuery(id+"F7.imprint","IMPRINT",FACE,{"disambiguationData":[TD([[makeQuery(id+"F7.imprint","IMPRINT",EDGE,{"derivedFrom":sQuery(id+"F7.wireOp",EDGE,"E70")}),-1.0]])]});
            extrude(context, id + "F18", {"entities" : qUnion([Q0, Q1, Q2, Q3]), "operationType" : NewBodyOperationType.REMOVE, "oppositeDirection" : true, "depth" : 4.83 * mm, "offsetDistance" : 25.4 * mm});
        }
        {
            var Q0;
            Q0=makeQuery(id+"F8.imprint","IMPRINT",FACE,{"disambiguationData":[TD([[makeQuery(id+"F8.imprint","IMPRINT",EDGE,{"derivedFrom":sQuery(id+"F8.wireOp",EDGE,"E92")}),-1.0]])]});
            var Q1;
            Q1=makeQuery(id+"F8.imprint","IMPRINT",FACE,{"disambiguationData":[TD([[makeQuery(id+"F8.imprint","IMPRINT",EDGE,{"derivedFrom":sQuery(id+"F8.wireOp",EDGE,"E94.MirrorC")}),1.0]])]});
            var Q2;
            Q2=makeQuery(id+"F8.imprint","IMPRINT",FACE,{"disambiguationData":[TD([[makeQuery(id+"F8.imprint","IMPRINT",EDGE,{"derivedFrom":sQuery(id+"F8.wireOp",EDGE,"E95.MirrorC")}),-1.0]])]});
            var Q3;
            Q3=makeQuery(id+"F8.imprint","IMPRINT",FACE,{"disambiguationData":[TD([[makeQuery(id+"F8.imprint","IMPRINT",EDGE,{"derivedFrom":sQuery(id+"F8.wireOp",EDGE,"E93.MirrorC")}),1.0]])]});
            extrude(context, id + "F19", {"entities" : qUnion([Q0, Q1, Q2, Q3]), "operationType" : NewBodyOperationType.REMOVE, "oppositeDirection" : true, "depth" : 4.83 * mm, "offsetDistance" : 25.4 * mm});
        }
        {
            var Q0;
            Q0=makeQuery(id+"F5.imprint","IMPRINT",FACE,{"disambiguationData":[TD([[makeQuery(id+"F5.imprint","IMPRINT",EDGE,{"derivedFrom":sQuery(id+"F5.wireOp",EDGE,"E23")}),-1.0]])]});
            var Q1;
            Q1=makeQuery(id+"F5.imprint","IMPRINT",FACE,{"disambiguationData":[TD([[makeQuery(id+"F5.imprint","IMPRINT",EDGE,{"derivedFrom":sQuery(id+"F5.wireOp",EDGE,"E25.MirrorC")}),1.0]])]});
            var Q2;
            Q2=makeQuery(id+"F5.imprint","IMPRINT",FACE,{"disambiguationData":[TD([[makeQuery(id+"F5.imprint","IMPRINT",EDGE,{"derivedFrom":sQuery(id+"F5.wireOp",EDGE,"E26.MirrorC")}),-1.0]])]});
            var Q3;
            Q3=makeQuery(id+"F5.imprint","IMPRINT",FACE,{"disambiguationData":[TD([[makeQuery(id+"F5.imprint","IMPRINT",EDGE,{"derivedFrom":sQuery(id+"F5.wireOp",EDGE,"E24.MirrorC")}),1.0]])]});
            extrude(context, id + "F20", {"entities" : qUnion([Q0, Q1, Q2, Q3]), "operationType" : NewBodyOperationType.REMOVE, "oppositeDirection" : true, "depth" : 4.83 * mm, "offsetDistance" : 25.4 * mm});
        }
        {
            var Q0;
            Q0=makeQuery(id+"F6.imprint","IMPRINT",FACE,{"disambiguationData":[TD([[makeQuery(id+"F6.imprint","IMPRINT",EDGE,{"derivedFrom":sQuery(id+"F6.wireOp",EDGE,"E45")}),-1.0]])]});
            var Q1;
            Q1=makeQuery(id+"F6.imprint","IMPRINT",FACE,{"disambiguationData":[TD([[makeQuery(id+"F6.imprint","IMPRINT",EDGE,{"derivedFrom":sQuery(id+"F6.wireOp",EDGE,"E47.MirrorC")}),1.0]])]});
            var Q2;
            Q2=makeQuery(id+"F6.imprint","IMPRINT",FACE,{"disambiguationData":[TD([[makeQuery(id+"F6.imprint","IMPRINT",EDGE,{"derivedFrom":sQuery(id+"F6.wireOp",EDGE,"E48.MirrorC")}),-1.0]])]});
            var Q3;
            Q3=makeQuery(id+"F6.imprint","IMPRINT",FACE,{"disambiguationData":[TD([[makeQuery(id+"F6.imprint","IMPRINT",EDGE,{"derivedFrom":sQuery(id+"F6.wireOp",EDGE,"E46.MirrorC")}),1.0]])]});
            extrude(context, id + "F21", {"entities" : qUnion([Q0, Q1, Q2, Q3]), "operationType" : NewBodyOperationType.REMOVE, "oppositeDirection" : true, "depth" : 4.83 * mm, "offsetDistance" : 25.4 * mm});
        }
        {
            var Q0;
            {var subQ5=sQuery(id+"F5.wireOp",EDGE,"E36.MirrorCS");Q0=makeQuery(id+"F5.imprint","IMPRINT",FACE,{"disambiguationData":[TD([[makeQuery(id+"F5.imprint","IMPRINT",EDGE,{"derivedFrom":subQ5}),-1.0]])]});}
            extrude(context, id + "F22", {"entities" : qUnion([Q0]), "operationType" : NewBodyOperationType.REMOVE, "oppositeDirection" : true, "depth" : 11.18 * mm, "offsetDistance" : 25.4 * mm});
        }
        {
            var Q0;
            {var subQ5=sQuery(id+"F6.wireOp",EDGE,"E58.MirrorCS");Q0=makeQuery(id+"F6.imprint","IMPRINT",FACE,{"disambiguationData":[TD([[makeQuery(id+"F6.imprint","IMPRINT",EDGE,{"derivedFrom":subQ5}),-1.0]])]});}
            extrude(context, id + "F23", {"entities" : qUnion([Q0]), "operationType" : NewBodyOperationType.REMOVE, "oppositeDirection" : true, "depth" : 11.18 * mm, "offsetDistance" : 25.4 * mm});
        }
        {
            var Q0;
            {var subQ5=sQuery(id+"F7.wireOp",EDGE,"E83.MirrorCS");Q0=makeQuery(id+"F7.imprint","IMPRINT",FACE,{"disambiguationData":[TD([[makeQuery(id+"F7.imprint","IMPRINT",EDGE,{"derivedFrom":subQ5}),-1.0]])]});}
            extrude(context, id + "F24", {"entities" : qUnion([Q0]), "operationType" : NewBodyOperationType.REMOVE, "oppositeDirection" : true, "depth" : 11.18 * mm, "offsetDistance" : 25.4 * mm});
        }
        {
            var Q0;
            {var subQ5=sQuery(id+"F8.wireOp",EDGE,"E105.MirrorCS");Q0=makeQuery(id+"F8.imprint","IMPRINT",FACE,{"disambiguationData":[TD([[makeQuery(id+"F8.imprint","IMPRINT",EDGE,{"derivedFrom":subQ5}),-1.0]])]});}
            extrude(context, id + "F25", {"entities" : qUnion([Q0]), "operationType" : NewBodyOperationType.REMOVE, "oppositeDirection" : true, "depth" : 11.18 * mm, "offsetDistance" : 25.4 * mm});
        }
        {
            var Q0;
            {var subQ0=sQuery(id+"F2.wireOp",EDGE,"E17.MirrorCS");Q0=makeQuery(id+"F2.imprint","IMPRINT",FACE,{"disambiguationData":[TD([[makeQuery(id+"F2.imprint","IMPRINT",EDGE,{"derivedFrom":subQ0}),-1.0]])]});}
            var Q1;
            {var subQ5=sQuery(id+"F2.wireOp",EDGE,"E19.MirrorCS");Q1=makeQuery(id+"F2.imprint","IMPRINT",FACE,{"disambiguationData":[TD([[makeQuery(id+"F2.imprint","IMPRINT",EDGE,{"derivedFrom":subQ5}),-1.0]])]});}
            extrude(context, id + "F26", {"entities" : qUnion([Q0, Q1]), "operationType" : NewBodyOperationType.REMOVE, "oppositeDirection" : true, "depth" : 11.18 * mm, "offsetDistance" : 25.4 * mm});
        }
    });
